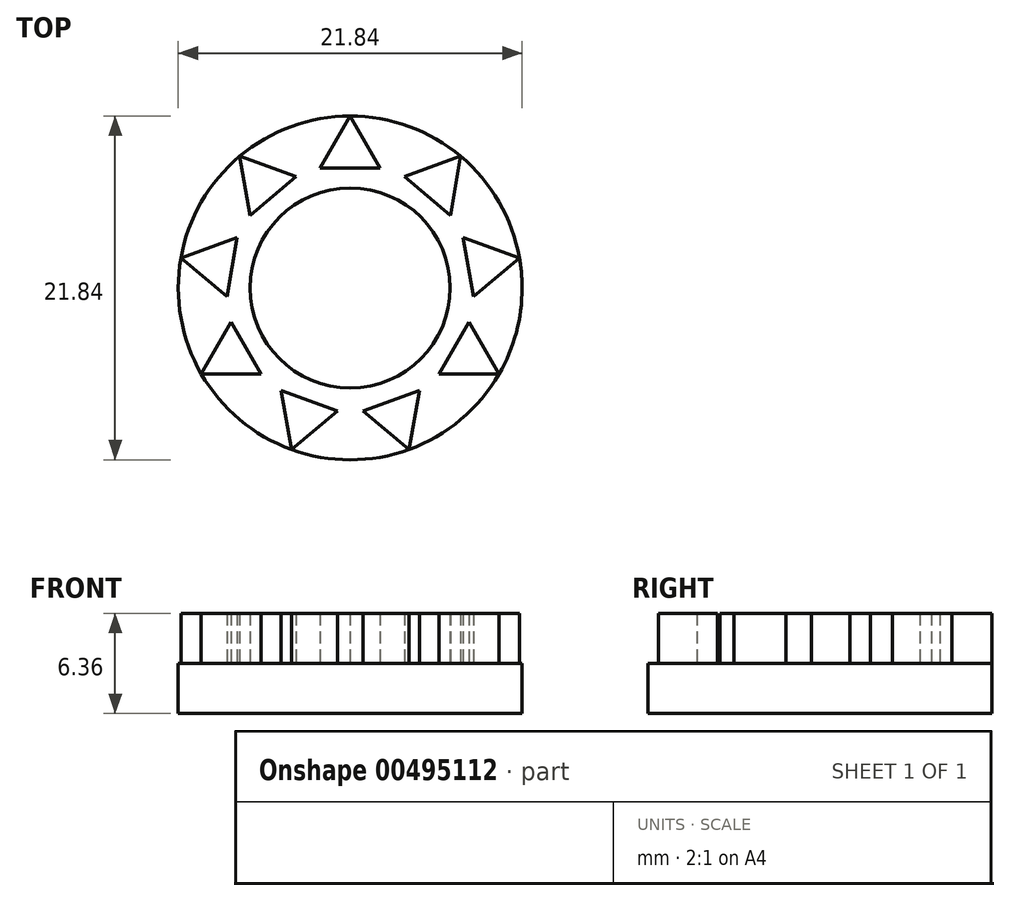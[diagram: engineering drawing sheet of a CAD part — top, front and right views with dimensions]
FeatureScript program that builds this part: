
annotation { "Feature Type Name" : "Feature", "Feature Type Description" : "" }
export const myFeature = defineFeature(function(context is Context, id is Id, definition is map)
    precondition{}
    {
        {
            var Q0;
            Q0=qCreatedBy(makeId("Top.planeOp"),FACE);
            var sketch = newSketch(context, id + "F0", { "sketchPlane" : qUnion([Q0])});
            skCircle(sketch, "E0", {"center": v(0, 0) * mm, "radius": 6.35 * mm});
            skLineSegment(sketch, "E1", {"start": v(-1.9, 7.62) * mm, "end": v(1.9, 7.62) * mm});
            skLineSegment(sketch, "E2", {"start": v(1.9, 7.62) * mm, "end": v(0, 10.92) * mm});
            skLineSegment(sketch, "E3", {"start": v(0, 10.92) * mm, "end": v(-1.9, 7.62) * mm});
            skCircle(sketch, "E4", {"center": v(0, 0) * mm, "radius": 10.92 * mm});
            skLineSegment(sketch, "E5.1.0", {"start": v(-3.44, 7.06) * mm, "end": v(-7.02, 8.36) * mm});
            skLineSegment(sketch, "E5.1.1", {"start": v(-7.02, 8.36) * mm, "end": v(-6.36, 4.61) * mm});
            skLineSegment(sketch, "E5.1.2", {"start": v(-6.36, 4.61) * mm, "end": v(-3.44, 7.06) * mm});
            skLineSegment(sketch, "E5.2.0", {"start": v(-7.17, 3.2) * mm, "end": v(-10.75, 1.9) * mm});
            skLineSegment(sketch, "E5.2.1", {"start": v(-10.75, 1.9) * mm, "end": v(-7.84, -0.55) * mm});
            skLineSegment(sketch, "E5.2.2", {"start": v(-7.84, -0.55) * mm, "end": v(-7.17, 3.2) * mm});
            skLineSegment(sketch, "E5.3.0", {"start": v(-7.55, -2.16) * mm, "end": v(-9.46, -5.46) * mm});
            skLineSegment(sketch, "E5.3.1", {"start": v(-9.46, -5.46) * mm, "end": v(-5.65, -5.46) * mm});
            skLineSegment(sketch, "E5.3.2", {"start": v(-5.65, -5.46) * mm, "end": v(-7.55, -2.16) * mm});
            skLineSegment(sketch, "E5.4.0", {"start": v(-4.4, -6.5) * mm, "end": v(-3.73, -10.26) * mm});
            skLineSegment(sketch, "E5.4.1", {"start": v(-3.73, -10.26) * mm, "end": v(-0.82, -7.81) * mm});
            skLineSegment(sketch, "E5.4.2", {"start": v(-0.82, -7.81) * mm, "end": v(-4.4, -6.5) * mm});
            skLineSegment(sketch, "E5.5.0", {"start": v(0.82, -7.81) * mm, "end": v(3.73, -10.26) * mm});
            skLineSegment(sketch, "E5.5.1", {"start": v(3.73, -10.26) * mm, "end": v(4.4, -6.5) * mm});
            skLineSegment(sketch, "E5.5.2", {"start": v(4.4, -6.5) * mm, "end": v(0.82, -7.81) * mm});
            skLineSegment(sketch, "E5.6.0", {"start": v(5.65, -5.46) * mm, "end": v(9.46, -5.46) * mm});
            skLineSegment(sketch, "E5.6.1", {"start": v(9.46, -5.46) * mm, "end": v(7.55, -2.16) * mm});
            skLineSegment(sketch, "E5.6.2", {"start": v(7.55, -2.16) * mm, "end": v(5.65, -5.46) * mm});
            skLineSegment(sketch, "E5.7.0", {"start": v(7.84, -0.55) * mm, "end": v(10.75, 1.9) * mm});
            skLineSegment(sketch, "E5.7.1", {"start": v(10.75, 1.9) * mm, "end": v(7.17, 3.2) * mm});
            skLineSegment(sketch, "E5.7.2", {"start": v(7.17, 3.2) * mm, "end": v(7.84, -0.55) * mm});
            skLineSegment(sketch, "E5.8.0", {"start": v(6.36, 4.61) * mm, "end": v(7.02, 8.36) * mm});
            skLineSegment(sketch, "E5.8.1", {"start": v(7.02, 8.36) * mm, "end": v(3.44, 7.06) * mm});
            skLineSegment(sketch, "E5.8.2", {"start": v(3.44, 7.06) * mm, "end": v(6.36, 4.61) * mm});
            skSolve(sketch);
        }
        {
            var Q0;
            Q0=makeQuery(id+"F0.imprint","IMPRINT",FACE,{"disambiguationData":[TD([[makeQuery(id+"F0.imprint","IMPRINT",EDGE,{"derivedFrom":sQuery(id+"F0.wireOp",EDGE,"E5.1.0")}),1.0]])]});
            var Q1;
            Q1=makeQuery(id+"F0.imprint","IMPRINT",FACE,{"disambiguationData":[TD([[makeQuery(id+"F0.imprint","IMPRINT",EDGE,{"derivedFrom":sQuery(id+"F0.wireOp",EDGE,"E1")}),1.0]])]});
            var Q2;
            Q2=makeQuery(id+"F0.imprint","IMPRINT",FACE,{"disambiguationData":[TD([[makeQuery(id+"F0.imprint","IMPRINT",EDGE,{"derivedFrom":sQuery(id+"F0.wireOp",EDGE,"E5.8.0")}),1.0]])]});
            var Q3;
            Q3=makeQuery(id+"F0.imprint","IMPRINT",FACE,{"disambiguationData":[TD([[makeQuery(id+"F0.imprint","IMPRINT",EDGE,{"derivedFrom":sQuery(id+"F0.wireOp",EDGE,"E5.7.0")}),1.0]])]});
            var Q4;
            Q4=makeQuery(id+"F0.imprint","IMPRINT",FACE,{"disambiguationData":[TD([[makeQuery(id+"F0.imprint","IMPRINT",EDGE,{"derivedFrom":sQuery(id+"F0.wireOp",EDGE,"E5.6.0")}),1.0]])]});
            var Q5;
            Q5=makeQuery(id+"F0.imprint","IMPRINT",FACE,{"disambiguationData":[TD([[makeQuery(id+"F0.imprint","IMPRINT",EDGE,{"derivedFrom":sQuery(id+"F0.wireOp",EDGE,"E5.5.0")}),1.0]])]});
            var Q6;
            Q6=makeQuery(id+"F0.imprint","IMPRINT",FACE,{"disambiguationData":[TD([[makeQuery(id+"F0.imprint","IMPRINT",EDGE,{"derivedFrom":sQuery(id+"F0.wireOp",EDGE,"E5.4.0")}),1.0]])]});
            var Q7;
            Q7=makeQuery(id+"F0.imprint","IMPRINT",FACE,{"disambiguationData":[TD([[makeQuery(id+"F0.imprint","IMPRINT",EDGE,{"derivedFrom":sQuery(id+"F0.wireOp",EDGE,"E5.3.0")}),1.0]])]});
            var Q8;
            Q8=makeQuery(id+"F0.imprint","IMPRINT",FACE,{"disambiguationData":[TD([[makeQuery(id+"F0.imprint","IMPRINT",EDGE,{"derivedFrom":sQuery(id+"F0.wireOp",EDGE,"E5.2.0")}),1.0]])]});
            var Q9;
            Q9=makeQuery(id+"F0.imprint","IMPRINT",FACE,{"disambiguationData":[TD([[makeQuery(id+"F0.imprint","IMPRINT",EDGE,{"derivedFrom":sQuery(id+"F0.wireOp",EDGE,"E0")}),1.0]])]});
            var Q10;
            Q10=makeQuery(id+"F0.imprint","IMPRINT",FACE,{"disambiguationData":[TD([[makeQuery(id+"F0.imprint","IMPRINT",EDGE,{"derivedFrom":sQuery(id+"F0.wireOp",EDGE,"E0")}),-1.0]])]});
            extrude(context, id + "F1", {"entities" : qUnion([Q0, Q1, Q2, Q3, Q4, Q5, Q6, Q7, Q8, Q9, Q10]), "oppositeDirection" : true, "depth" : 3.17 * mm});
        }
        {
            var Q0;
            Q0=makeQuery(id+"F0.imprint","IMPRINT",FACE,{"disambiguationData":[TD([[makeQuery(id+"F0.imprint","IMPRINT",EDGE,{"derivedFrom":sQuery(id+"F0.wireOp",EDGE,"E5.2.0")}),1.0]])]});
            var Q1;
            Q1=makeQuery(id+"F0.imprint","IMPRINT",FACE,{"disambiguationData":[TD([[makeQuery(id+"F0.imprint","IMPRINT",EDGE,{"derivedFrom":sQuery(id+"F0.wireOp",EDGE,"E1")}),1.0]])]});
            var Q2;
            Q2=makeQuery(id+"F0.imprint","IMPRINT",FACE,{"disambiguationData":[TD([[makeQuery(id+"F0.imprint","IMPRINT",EDGE,{"derivedFrom":sQuery(id+"F0.wireOp",EDGE,"E5.8.0")}),1.0]])]});
            var Q3;
            Q3=makeQuery(id+"F0.imprint","IMPRINT",FACE,{"disambiguationData":[TD([[makeQuery(id+"F0.imprint","IMPRINT",EDGE,{"derivedFrom":sQuery(id+"F0.wireOp",EDGE,"E5.7.0")}),1.0]])]});
            var Q4;
            Q4=makeQuery(id+"F0.imprint","IMPRINT",FACE,{"disambiguationData":[TD([[makeQuery(id+"F0.imprint","IMPRINT",EDGE,{"derivedFrom":sQuery(id+"F0.wireOp",EDGE,"E5.6.0")}),1.0]])]});
            var Q5;
            Q5=makeQuery(id+"F0.imprint","IMPRINT",FACE,{"disambiguationData":[TD([[makeQuery(id+"F0.imprint","IMPRINT",EDGE,{"derivedFrom":sQuery(id+"F0.wireOp",EDGE,"E5.5.0")}),1.0]])]});
            var Q6;
            Q6=makeQuery(id+"F0.imprint","IMPRINT",FACE,{"disambiguationData":[TD([[makeQuery(id+"F0.imprint","IMPRINT",EDGE,{"derivedFrom":sQuery(id+"F0.wireOp",EDGE,"E5.4.0")}),1.0]])]});
            var Q7;
            Q7=makeQuery(id+"F0.imprint","IMPRINT",FACE,{"disambiguationData":[TD([[makeQuery(id+"F0.imprint","IMPRINT",EDGE,{"derivedFrom":sQuery(id+"F0.wireOp",EDGE,"E5.3.0")}),1.0]])]});
            var Q8;
            Q8=makeQuery(id+"F0.imprint","IMPRINT",FACE,{"disambiguationData":[TD([[makeQuery(id+"F0.imprint","IMPRINT",EDGE,{"derivedFrom":sQuery(id+"F0.wireOp",EDGE,"E5.1.0")}),1.0]])]});
            var Q9;
            Q9=makeQuery(id+"F0.imprint","IMPRINT",FACE,{"disambiguationData":[TD([[makeQuery(id+"F0.imprint","IMPRINT",EDGE,{"derivedFrom":sQuery(id+"F0.wireOp",EDGE,"E0")}),1.0]])]});
            extrude(context, id + "F2", {"entities" : qUnion([Q0, Q1, Q2, Q3, Q4, Q5, Q6, Q7, Q8, Q9]), "operationType" : NewBodyOperationType.ADD, "depth" : 3.17 * mm});
        }
    });
